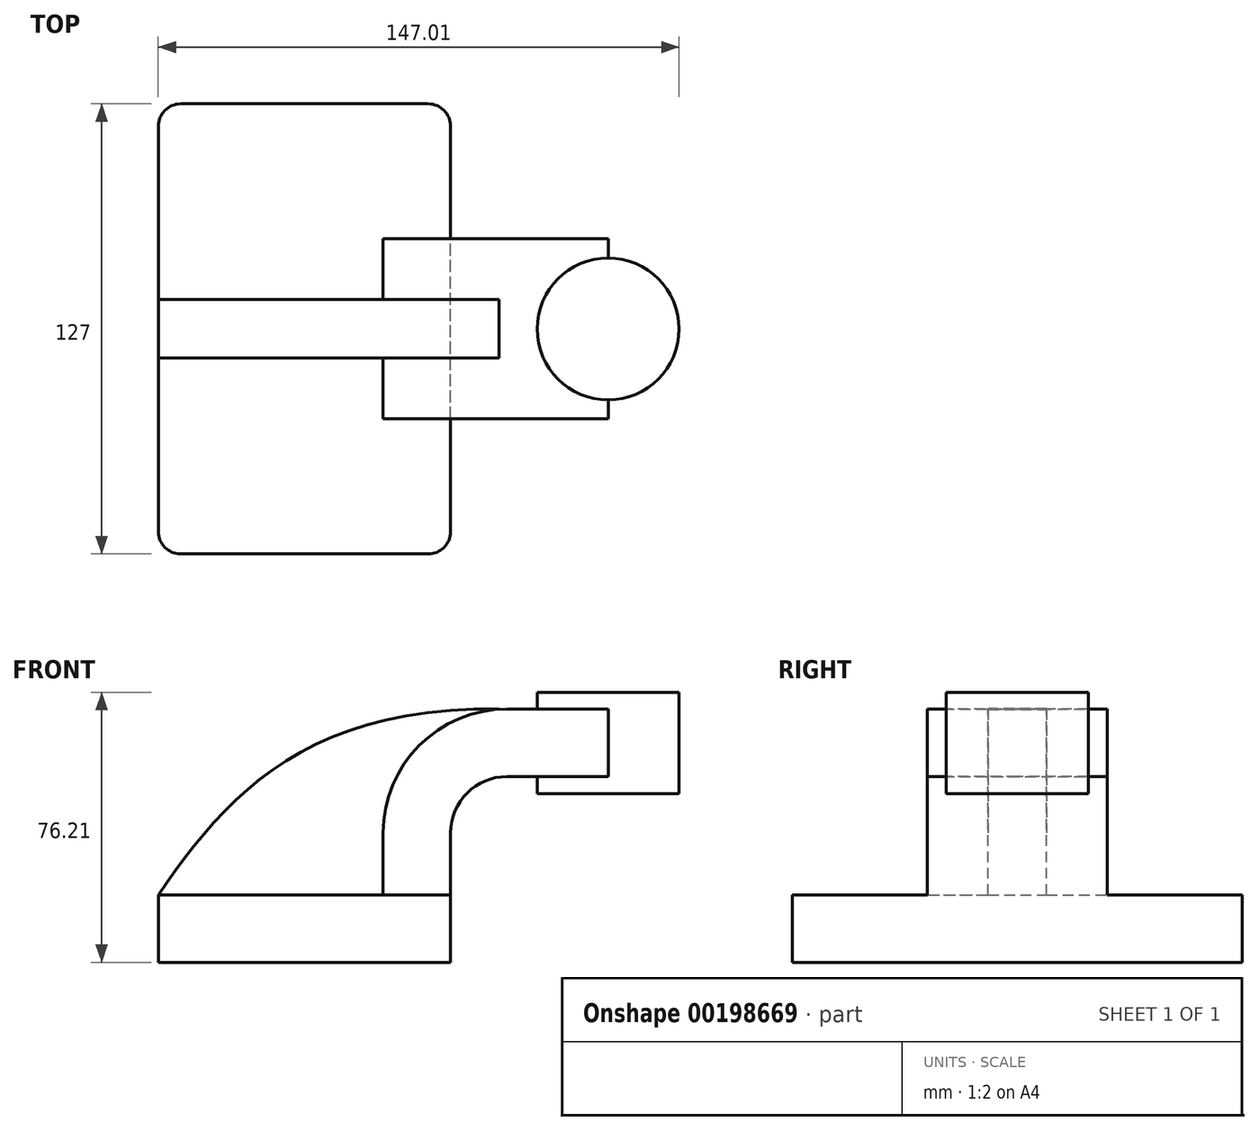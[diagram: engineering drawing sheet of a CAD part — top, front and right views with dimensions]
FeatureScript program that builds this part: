
annotation { "Feature Type Name" : "Feature", "Feature Type Description" : "" }
export const myFeature = defineFeature(function(context is Context, id is Id, definition is map)
    precondition{}
    {
        {
            var Q0;
            Q0=qCreatedBy(makeId("Front.planeOp"),FACE);
            var sketch = newSketch(context, id + "F0", { "sketchPlane" : qUnion([Q0])});
            skLineSegment(sketch, "E0.bottom", {"start": v(41.27, 9.53) * mm, "end": v(-41.28, 9.53) * mm});
            skLineSegment(sketch, "E0.top", {"start": v(41.28, -9.52) * mm, "end": v(-41.27, -9.52) * mm});
            skLineSegment(sketch, "E0.left", {"start": v(41.28, 9.53) * mm, "end": v(41.28, -9.52) * mm});
            skLineSegment(sketch, "E0.right", {"start": v(-41.28, 9.53) * mm, "end": v(-41.28, -9.52) * mm});
            skPoint(sketch, "E0.middle", {"position": v(0, 0) * mm});
            skLineSegment(sketch, "E1.bottom", {"start": v(54.93, 38.1) * mm, "end": v(105.73, 38.1) * mm});
            skLineSegment(sketch, "E1.top", {"start": v(54.93, 66.68) * mm, "end": v(105.73, 66.68) * mm});
            skLineSegment(sketch, "E1.left", {"start": v(54.93, 38.1) * mm, "end": v(54.93, 66.68) * mm});
            skLineSegment(sketch, "E1.right", {"start": v(105.73, 38.1) * mm, "end": v(105.73, 66.68) * mm});
            skPoint(sketch, "E1.middle", {"position": v(80.33, 52.39) * mm});
            skLineSegment(sketch, "E2", {"start": v(41.27, 9.53) * mm, "end": v(41.27, 27) * mm});
            skArc(sketch, "E3", {"start": v(41.27, 27) * mm, "mid": v(45.92, 38.23) * mm, "end": v(57.15, 42.88) * mm});
            skLineSegment(sketch, "E4", {"start": v(57.15, 42.88) * mm, "end": v(85.72, 42.88) * mm});
            skLineSegment(sketch, "E5.0", {"start": v(57.15, 61.93) * mm, "end": v(85.72, 61.93) * mm});
            skArc(sketch, "E5.1", {"start": v(22.22, 27) * mm, "mid": v(32.45, 51.7) * mm, "end": v(57.15, 61.93) * mm});
            skLineSegment(sketch, "E5.2", {"start": v(22.22, 9.53) * mm, "end": v(22.22, 27) * mm});
            skLineSegment(sketch, "E6", {"start": v(85.72, 38.1) * mm, "end": v(85.72, 66.68) * mm});
            skFitSpline(sketch, "E7", {"points": [v(-41.28, 9.53) * mm, v(57.15, 61.93) * mm], "startDerivative": vector(56, 81.33) * mm, "endDerivative": vector(171.45, -4.59) * mm});
            skSolve(sketch);
        }
        {
            var Q0;
            Q0=makeQuery(id+"F0.imprint","IMPRINT",FACE,{"disambiguationData":[TD([[makeQuery(id+"F0.imprint","IMPRINT",EDGE,{"derivedFrom":sQuery(id+"F0.wireOp",EDGE,"E0.top")}),-1.0]])]});
            extrude(context, id + "F1", {"entities" : qUnion([Q0]), "endBound" : BoundingType.SYMMETRIC, "depth" : 127 * mm});
        }
        {
            var Q0;
            {var subQ1=sQuery(id+"F0.wireOp",EDGE,"E2");Q0=makeQuery(id+"F0.imprint","IMPRINT",FACE,{"disambiguationData":[TD([[makeQuery(id+"F0.imprint","IMPRINT",EDGE,{"derivedFrom":subQ1}),1.0]])]});}
            var Q1;
            {var subQ1=sQuery(id+"F0.wireOp",EDGE,"E4");Q1=makeQuery(id+"F0.imprint","IMPRINT",FACE,{"disambiguationData":[TD([[makeQuery(id+"F0.imprint","IMPRINT",EDGE,{"derivedFrom":subQ1}),1.0]])]});}
            extrude(context, id + "F2", {"entities" : qUnion([Q0, Q1]), "operationType" : NewBodyOperationType.ADD, "endBound" : BoundingType.SYMMETRIC, "depth" : 50.8 * mm});
        }
        {
            var Q0;
            {var subQ0=sQuery(id+"F0.wireOp",EDGE,"E5.2");Q0=makeQuery(id+"F0.imprint","IMPRINT",FACE,{"disambiguationData":[TD([[makeQuery(id+"F0.imprint","IMPRINT",EDGE,{"derivedFrom":subQ0}),1.0]])]});}
            extrude(context, id + "F3", {"entities" : qUnion([Q0]), "operationType" : NewBodyOperationType.ADD, "endBound" : BoundingType.SYMMETRIC, "depth" : 16.5 * mm});
        }
        {
            var Q0;
            {var subQ0=sQuery(id+"F0.wireOp",EDGE,"E1.right");Q0=makeQuery(id+"F0.imprint","IMPRINT",FACE,{"disambiguationData":[TD([[makeQuery(id+"F0.imprint","IMPRINT",EDGE,{"derivedFrom":subQ0}),1.0]])]});}
            var Q1;
            Q1=sQuery(id+"F0.wireOp",EDGE,"E6");
            revolve(context, id + "F4", {"operationType" : NewBodyOperationType.ADD, "entities" : qUnion([Q0]), "axis" : qUnion([Q1]), "revolveType" : RevolveType.FULL});
        }
        {
            var Q0;
            Q0=makeQuery(id+"F1.opExtrude","CAP_EDGE",EDGE,{"disambiguationData":[OSD([sQuery(id+"F0.wireOp",EDGE,"E0.left")])],"isStart":false});
            var Q1;
            Q1=makeQuery(id+"F1.opExtrude","CAP_EDGE",EDGE,{"disambiguationData":[OSD([sQuery(id+"F0.wireOp",EDGE,"E0.right")])],"isStart":false});
            var Q2;
            Q2=makeQuery(id+"F1.opExtrude","CAP_EDGE",EDGE,{"disambiguationData":[OSD([sQuery(id+"F0.wireOp",EDGE,"E0.right")])],"isStart":true});
            var Q3;
            Q3=makeQuery(id+"F1.opExtrude","CAP_EDGE",EDGE,{"disambiguationData":[OSD([sQuery(id+"F0.wireOp",EDGE,"E0.left")])],"isStart":true});
            fillet(context, id + "F5", {"entities" : qUnion([Q0, Q1, Q2, Q3]), "radius" : 6.35 * mm, "tangentPropagation" : true, "allowEdgeOverflow" : false});
        }
    });
